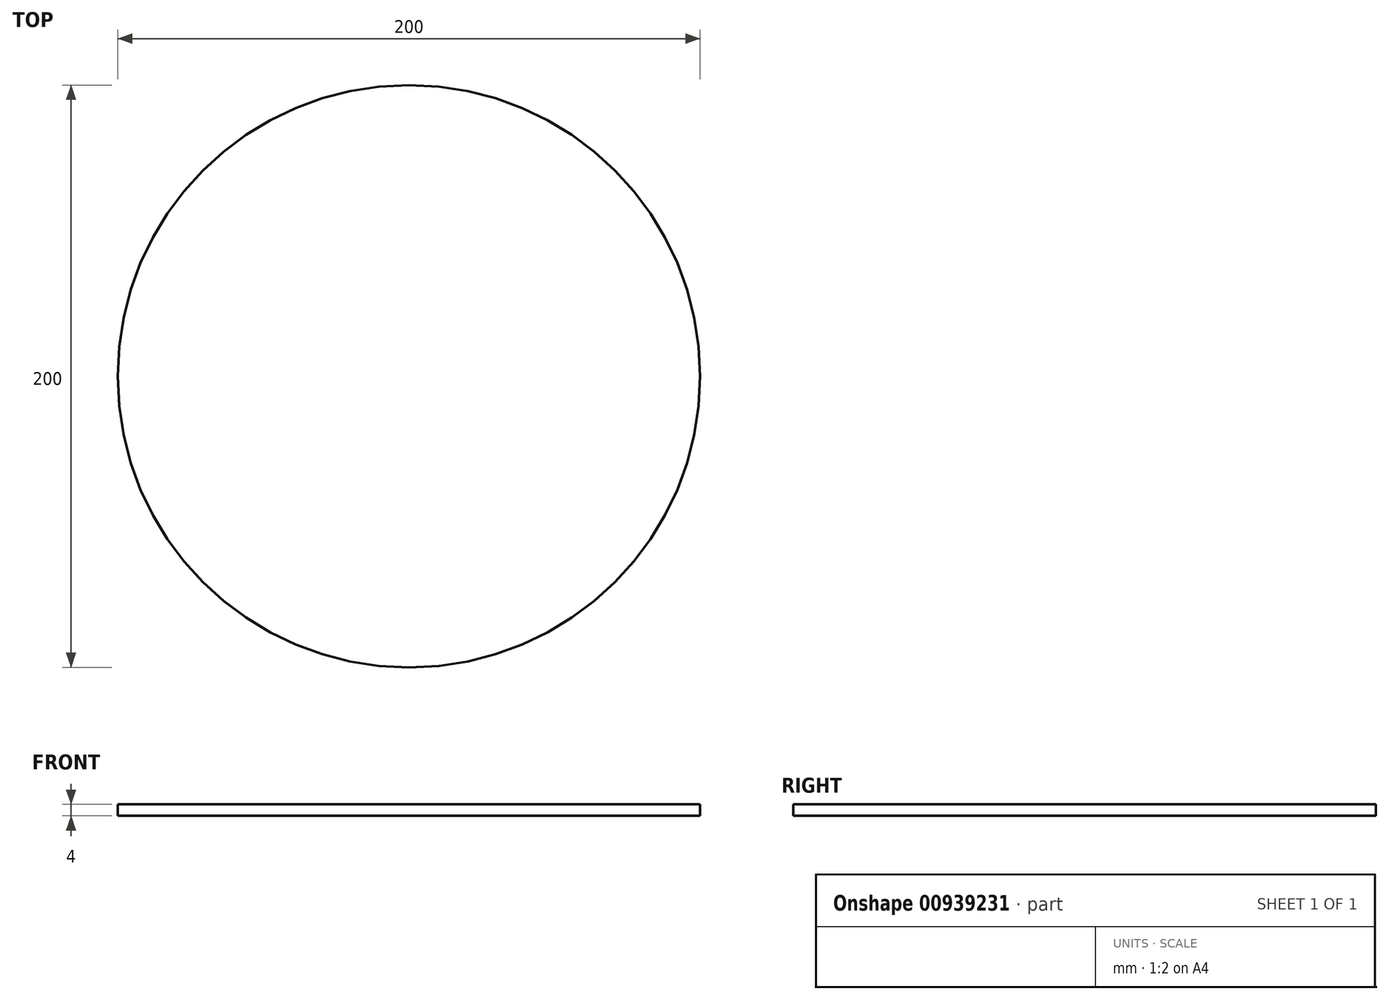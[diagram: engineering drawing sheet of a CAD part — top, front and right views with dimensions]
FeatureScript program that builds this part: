
annotation { "Feature Type Name" : "Feature", "Feature Type Description" : "" }
export const myFeature = defineFeature(function(context is Context, id is Id, definition is map)
    precondition{}
    {
        {
            var Q0;
            Q0=qCreatedBy(makeId("Top.planeOp"),FACE);
            var sketch = newSketch(context, id + "F0", { "sketchPlane" : qUnion([Q0])});
            skCircle(sketch, "E0", {"center": v(0, 0) * mm, "radius": 100 * mm});
            skSolve(sketch);
        }
        {
            var Q0;
            Q0=makeQuery(id+"F0.imprint","IMPRINT",FACE,{"disambiguationData":[TD([[makeQuery(id+"F0.imprint","IMPRINT",EDGE,{"derivedFrom":sQuery(id+"F0.wireOp",EDGE,"E0")}),1.0]])]});
            extrude(context, id + "F1", {"entities" : qUnion([Q0]), "depth" : 4 * mm, "offsetDistance" : 25 * mm});
        }
    });
